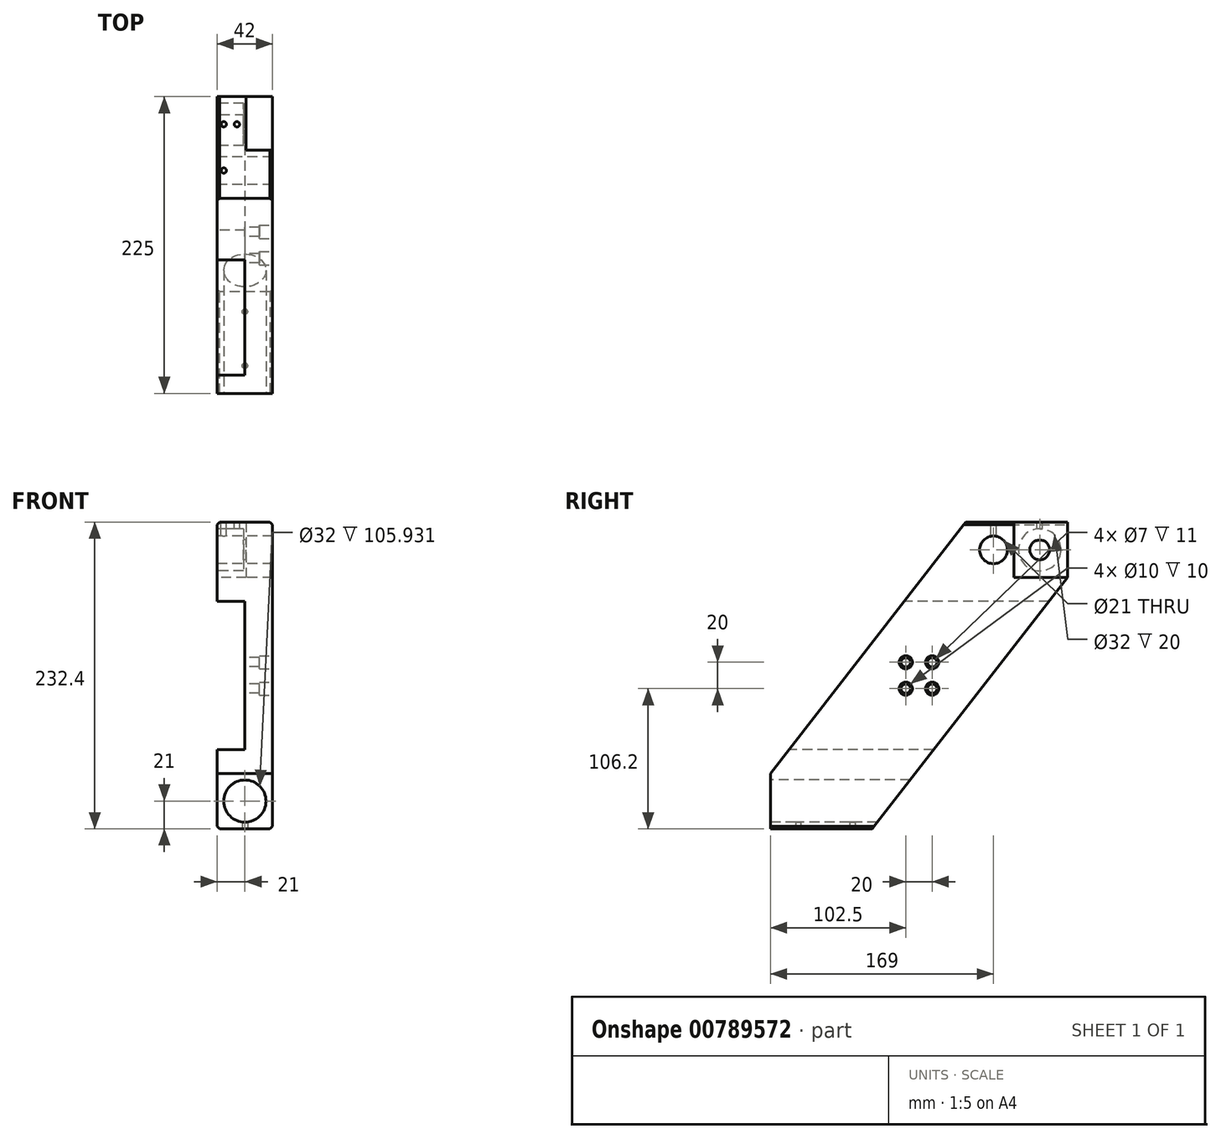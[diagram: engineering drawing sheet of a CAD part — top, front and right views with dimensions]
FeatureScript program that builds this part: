
annotation { "Feature Type Name" : "Feature", "Feature Type Description" : "" }
export const myFeature = defineFeature(function(context is Context, id is Id, definition is map)
    precondition{}
    {
        {
            var Q0;
            Q0=qCreatedBy(makeId("Right.planeOp"),FACE);
            var sketch = newSketch(context, id + "F0", { "sketchPlane" : qUnion([Q0])});
            skLineSegment(sketch, "E0.bottom", {"start": v(112.5, 116.2) * mm, "end": v(35.5, 116.2) * mm});
            skLineSegment(sketch, "E0.top", {"start": v(112.5, -116.2) * mm, "end": v(70.5, -116.2) * mm});
            skLineSegment(sketch, "E0.left", {"start": v(112.5, 116.2) * mm, "end": v(112.5, 74.2) * mm});
            skLineSegment(sketch, "E0.right", {"start": v(-112.5, 116.2) * mm, "end": v(-112.5, 74.2) * mm});
            skCircle(sketch, "E1", {"center": v(56.5, 95.2) * mm, "radius": 10.5 * mm});
            skCircle(sketch, "E2", {"center": v(-91.5, 95.2) * mm, "radius": 10.5 * mm});
            skPoint(sketch, "E3", {"position": v(0, 0) * mm});
            skPoint(sketch, "E4.start.orphan", {"position": v(112.5, 116.2) * mm});
            skPoint(sketch, "E5.trimOffspring.end.orphan", {"position": v(-112.5, 116.2) * mm});
            skCircle(sketch, "E6", {"center": v(91.5, 95.2) * mm, "radius": 7.5 * mm});
            skPoint(sketch, "E7", {"position": v(-35.5, -116.2) * mm});
            skPoint(sketch, "E8", {"position": v(70.5, -116.2) * mm});
            skPoint(sketch, "E9", {"position": v(112.5, -74.2) * mm});
            skPoint(sketch, "E10", {"position": v(-112.5, -74.2) * mm});
            skPoint(sketch, "E11", {"position": v(112.5, 74.2) * mm});
            skPoint(sketch, "E12", {"position": v(-112.5, 74.2) * mm});
            skLineSegment(sketch, "E13", {"start": v(112.5, 74.2) * mm, "end": v(-35.5, -116.2) * mm});
            skLineSegment(sketch, "E14", {"start": v(70.5, -116.2) * mm, "end": v(-112.5, 74.2) * mm});
            skPoint(sketch, "E15", {"position": v(35.5, 116.2) * mm});
            skPoint(sketch, "E16", {"position": v(-70.5, 116.2) * mm});
            skLineSegment(sketch, "E17", {"start": v(35.5, 116.2) * mm, "end": v(-112.5, -74.2) * mm});
            skLineSegment(sketch, "E18", {"start": v(112.5, -74.2) * mm, "end": v(-70.5, 116.2) * mm});
            skLineSegment(sketch, "E19.trimOffspring", {"start": v(-70.5, 116.2) * mm, "end": v(-112.5, 116.2) * mm});
            skLineSegment(sketch, "E20.trimOffspring", {"start": v(-112.5, -74.2) * mm, "end": v(-112.5, -116.2) * mm});
            skLineSegment(sketch, "E21.trimOffspring", {"start": v(-35.5, -116.2) * mm, "end": v(-112.5, -116.2) * mm});
            skLineSegment(sketch, "E22.trimOffspring", {"start": v(112.5, -74.2) * mm, "end": v(112.5, -116.2) * mm});
            skPoint(sketch, "E23", {"position": v(10, 10) * mm});
            skPoint(sketch, "E24", {"position": v(10, -10) * mm});
            skPoint(sketch, "E25", {"position": v(-10, -10) * mm});
            skPoint(sketch, "E26", {"position": v(-10, 10) * mm});
            skCircle(sketch, "E27", {"center": v(10, 10) * mm, "radius": 3.5 * mm});
            skCircle(sketch, "E28", {"center": v(-10, 10) * mm, "radius": 3.5 * mm});
            skCircle(sketch, "E29", {"center": v(10, -10) * mm, "radius": 3.5 * mm});
            skCircle(sketch, "E30", {"center": v(-10, -10) * mm, "radius": 3.5 * mm});
            skLineSegment(sketch, "E31", {"start": v(-112.5, 116.2) * mm, "end": v(112.5, -116.2) * mm});
            skLineSegment(sketch, "E32", {"start": v(-112.5, -116.2) * mm, "end": v(112.5, 116.2) * mm});
            skSolve(sketch);
        }
        {
            var Q0;
            {var subQ5=sQuery(id+"F0.wireOp",EDGE,"E20.trimOffspring");Q0=makeQuery(id+"F0.imprint","IMPRINT",FACE,{"disambiguationData":[TD([[makeQuery(id+"F0.imprint","IMPRINT",EDGE,{"derivedFrom":subQ5}),1.0]])]});}
            var Q1;
            {var subQ0=sQuery(id+"F0.wireOp",EDGE,"E21.trimOffspring");Q1=makeQuery(id+"F0.imprint","IMPRINT",FACE,{"disambiguationData":[TD([[makeQuery(id+"F0.imprint","IMPRINT",EDGE,{"derivedFrom":subQ0}),-1.0]])]});}
            var Q2;
            {var subQ6=sQuery(id+"F0.wireOp",EDGE,"E17");var subQ7=sQuery(id+"F0.wireOp",EDGE,"E14");var subQ8=makeQuery(id+"F0.imprint","INTERSECT",VERTEX,{"derivedFrom":[subQ7,subQ6]});Q2=makeQuery(id+"F0.imprint","IMPRINT",FACE,{"disambiguationData":[TD([[makeQuery(id+"F0.imprint","IMPRINT",EDGE,{"disambiguationData":[TD([[subQ8,1.0]])],"derivedFrom":subQ7}),-1.0]])]});}
            var Q3;
            {var subQ4=sQuery(id+"F0.wireOp",EDGE,"E14");var subQ5=sQuery(id+"F0.wireOp",EDGE,"E13");var subQ6=makeQuery(id+"F0.imprint","INTERSECT",VERTEX,{"derivedFrom":[subQ5,subQ4]});Q3=makeQuery(id+"F0.imprint","IMPRINT",FACE,{"disambiguationData":[TD([[makeQuery(id+"F0.imprint","IMPRINT",EDGE,{"disambiguationData":[TD([[subQ6,1.0]])],"derivedFrom":subQ5}),-1.0]])]});}
            var Q4;
            {var subQ8=sQuery(id+"F0.wireOp",EDGE,"E18");var subQ9=sQuery(id+"F0.wireOp",EDGE,"E17");var subQ10=makeQuery(id+"F0.imprint","INTERSECT",VERTEX,{"derivedFrom":[subQ9,subQ8]});Q4=makeQuery(id+"F0.imprint","IMPRINT",FACE,{"disambiguationData":[TD([[makeQuery(id+"F0.imprint","IMPRINT",EDGE,{"disambiguationData":[TD([[subQ10,-1.0]])],"derivedFrom":subQ9}),1.0]])]});}
            var Q5;
            {var subQ4=sQuery(id+"F0.wireOp",EDGE,"E13");var subQ6=sQuery(id+"F0.wireOp",EDGE,"E18");var subQ7=makeQuery(id+"F0.imprint","INTERSECT",VERTEX,{"derivedFrom":[subQ4,subQ6]});Q5=makeQuery(id+"F0.imprint","IMPRINT",FACE,{"disambiguationData":[TD([[makeQuery(id+"F0.imprint","IMPRINT",EDGE,{"disambiguationData":[TD([[subQ7,-1.0]])],"derivedFrom":subQ4}),-1.0]])]});}
            var Q6;
            {var subQ1=sQuery(id+"F0.wireOp",EDGE,"E0.left");Q6=makeQuery(id+"F0.imprint","IMPRINT",FACE,{"disambiguationData":[TD([[makeQuery(id+"F0.imprint","IMPRINT",EDGE,{"derivedFrom":subQ1}),-1.0]])]});}
            var Q7;
            {var subQ1=sQuery(id+"F0.wireOp",EDGE,"E0.bottom");Q7=makeQuery(id+"F0.imprint","IMPRINT",FACE,{"disambiguationData":[TD([[makeQuery(id+"F0.imprint","IMPRINT",EDGE,{"derivedFrom":subQ1}),1.0]])]});}
            extrude(context, id + "F1", {"entities" : qUnion([Q0, Q1, Q2, Q3, Q4, Q5, Q6, Q7]), "depth" : 42 * mm, "offsetDistance" : 25 * mm});
        }
        {
            var Q0;
            Q0=makeQuery(id+"F1.opExtrude","CAP_FACE",FACE,{"disambiguationData":[OSD([sQuery(id+"F0.wireOp",EDGE,"E0.bottom"),sQuery(id+"F0.wireOp",EDGE,"E0.left"),sQuery(id+"F0.wireOp",EDGE,"E1"),sQuery(id+"F0.wireOp",EDGE,"E6"),sQuery(id+"F0.wireOp",EDGE,"E13"),sQuery(id+"F0.wireOp",EDGE,"E17"),sQuery(id+"F0.wireOp",EDGE,"E20.trimOffspring"),sQuery(id+"F0.wireOp",EDGE,"E21.trimOffspring"),sQuery(id+"F0.wireOp",EDGE,"E27"),sQuery(id+"F0.wireOp",EDGE,"E28"),sQuery(id+"F0.wireOp",EDGE,"E29"),sQuery(id+"F0.wireOp",EDGE,"E30")])],"isStart":false});
            var sketch = newSketch(context, id + "F2", { "sketchPlane" : qUnion([Q0])});
            skCircle(sketch, "E33", {"center": v(-10, 10) * mm, "radius": 5 * mm});
            skCircle(sketch, "E34", {"center": v(10, 10) * mm, "radius": 5 * mm});
            skCircle(sketch, "E35", {"center": v(10, -10) * mm, "radius": 5 * mm});
            skCircle(sketch, "E36", {"center": v(-10, -10) * mm, "radius": 5 * mm});
            skSolve(sketch);
        }
        {
            var Q0;
            Q0=makeQuery(id+"F2.imprint","IMPRINT",FACE,{"disambiguationData":[TD([[makeQuery(id+"F2.imprint","IMPRINT",EDGE,{"derivedFrom":sQuery(id+"F2.wireOp",EDGE,"E35")}),1.0]])]});
            var Q1;
            Q1=makeQuery(id+"F2.imprint","IMPRINT",FACE,{"disambiguationData":[TD([[makeQuery(id+"F2.imprint","IMPRINT",EDGE,{"derivedFrom":sQuery(id+"F2.wireOp",EDGE,"E36")}),1.0]])]});
            var Q2;
            Q2=makeQuery(id+"F2.imprint","IMPRINT",FACE,{"disambiguationData":[TD([[makeQuery(id+"F2.imprint","IMPRINT",EDGE,{"derivedFrom":sQuery(id+"F2.wireOp",EDGE,"E33")}),1.0]])]});
            var Q3;
            Q3=makeQuery(id+"F2.imprint","IMPRINT",FACE,{"disambiguationData":[TD([[makeQuery(id+"F2.imprint","IMPRINT",EDGE,{"derivedFrom":sQuery(id+"F2.wireOp",EDGE,"E34")}),1.0]])]});
            extrude(context, id + "F3", {"entities" : qUnion([Q0, Q1, Q2, Q3]), "operationType" : NewBodyOperationType.REMOVE, "oppositeDirection" : true, "depth" : 10 * mm, "offsetDistance" : 25 * mm});
        }
        {
            var Q0;
            Q0=makeQuery(id+"F1.opExtrude","CAP_FACE",FACE,{"disambiguationData":[OSD([sQuery(id+"F0.wireOp",EDGE,"E0.bottom"),sQuery(id+"F0.wireOp",EDGE,"E0.left"),sQuery(id+"F0.wireOp",EDGE,"E1"),sQuery(id+"F0.wireOp",EDGE,"E6"),sQuery(id+"F0.wireOp",EDGE,"E13"),sQuery(id+"F0.wireOp",EDGE,"E17"),sQuery(id+"F0.wireOp",EDGE,"E20.trimOffspring"),sQuery(id+"F0.wireOp",EDGE,"E21.trimOffspring"),sQuery(id+"F0.wireOp",EDGE,"E27"),sQuery(id+"F0.wireOp",EDGE,"E28"),sQuery(id+"F0.wireOp",EDGE,"E29"),sQuery(id+"F0.wireOp",EDGE,"E30")])],"isStart":false});
            var sketch = newSketch(context, id + "F4", { "sketchPlane" : qUnion([Q0])});
            skLineSegment(sketch, "E37", {"start": v(72, 116.2) * mm, "end": v(72, 74.2) * mm});
            skLineSegment(sketch, "E38", {"start": v(72, 74.2) * mm, "end": v(145, 74.2) * mm});
            skLineSegment(sketch, "E39", {"start": v(145, 74.2) * mm, "end": v(145, 116.2) * mm});
            skLineSegment(sketch, "E40", {"start": v(145, 116.2) * mm, "end": v(72, 116.2) * mm});
            skSolve(sketch);
        }
        {
            var Q0;
            {var subQ2=sQuery(id+"F4.wireOp",EDGE,"E37");Q0=makeQuery(id+"F4.imprint","IMPRINT",FACE,{"disambiguationData":[TD([[makeQuery(id+"F4.imprint","IMPRINT",EDGE,{"derivedFrom":subQ2}),1.0]])]});}
            extrude(context, id + "F5", {"entities" : qUnion([Q0]), "operationType" : NewBodyOperationType.REMOVE, "oppositeDirection" : true, "depth" : 20 * mm, "offsetDistance" : 25 * mm});
        }
        {
            var Q0;
            Q0=makeQuery(id+"F1.opExtrude","CAP_FACE",FACE,{"disambiguationData":[OSD([sQuery(id+"F0.wireOp",EDGE,"E0.bottom"),sQuery(id+"F0.wireOp",EDGE,"E0.left"),sQuery(id+"F0.wireOp",EDGE,"E1"),sQuery(id+"F0.wireOp",EDGE,"E6"),sQuery(id+"F0.wireOp",EDGE,"E13"),sQuery(id+"F0.wireOp",EDGE,"E17"),sQuery(id+"F0.wireOp",EDGE,"E20.trimOffspring"),sQuery(id+"F0.wireOp",EDGE,"E21.trimOffspring"),sQuery(id+"F0.wireOp",EDGE,"E27"),sQuery(id+"F0.wireOp",EDGE,"E28"),sQuery(id+"F0.wireOp",EDGE,"E29"),sQuery(id+"F0.wireOp",EDGE,"E30")])],"isStart":true});
            var sketch = newSketch(context, id + "F6", { "sketchPlane" : qUnion([Q0])});
            skLineSegment(sketch, "E41", {"start": v(-98.5, 56.2) * mm, "end": v(11.14, 56.2) * mm});
            skLineSegment(sketch, "E42", {"start": v(-11.14, -56.2) * mm, "end": v(112.5, -56.2) * mm});
            skSolve(sketch);
        }
        {
            var Q0;
            {var subQ1=sQuery(id+"F6.wireOp",EDGE,"E41");Q0=makeQuery(id+"F6.imprint","IMPRINT",FACE,{"disambiguationData":[TD([[makeQuery(id+"F6.imprint","IMPRINT",EDGE,{"derivedFrom":subQ1}),-1.0]])]});}
            extrude(context, id + "F7", {"entities" : qUnion([Q0]), "operationType" : NewBodyOperationType.REMOVE, "oppositeDirection" : true, "depth" : 21 * mm, "offsetDistance" : 25 * mm});
        }
        {
            var Q0;
            Q0=makeQuery(id+"F1.opExtrude","SWEPT_FACE",FACE,{"disambiguationData":[OSD([sQuery(id+"F0.wireOp",EDGE,"E20.trimOffspring")])]});
            var sketch = newSketch(context, id + "F8", { "sketchPlane" : qUnion([Q0])});
            skPoint(sketch, "E43", {"position": v(21, -95.2) * mm});
            skPoint(sketch, "E43.positionSnap0", {"position": v(42, -95.2) * mm});
            skCircle(sketch, "E44", {"center": v(21, -95.2) * mm, "radius": 16 * mm});
            skSolve(sketch);
        }
        {
            var Q0;
            Q0=makeQuery(id+"F8.imprint","IMPRINT",FACE,{"disambiguationData":[TD([[makeQuery(id+"F8.imprint","IMPRINT",EDGE,{"derivedFrom":sQuery(id+"F8.wireOp",EDGE,"E44")}),1.0]])]});
            extrude(context, id + "F9", {"entities" : qUnion([Q0]), "operationType" : NewBodyOperationType.REMOVE, "oppositeDirection" : true, "depth" : 150 * mm, "offsetDistance" : 25 * mm});
        }
        {
            var Q0;
            Q0=makeQuery(id+"F1.opExtrude","CAP_EDGE",EDGE,{"disambiguationData":[OSD([sQuery(id+"F0.wireOp",EDGE,"E21.trimOffspring")])],"isStart":false});
            var Q1;
            Q1=makeQuery(id+"F5.boolean.opBoolean","COPY",EDGE,{"derivedFrom":makeQuery(id+"F5.opExtrude","CAP_EDGE",EDGE,{"disambiguationData":[OSD([sQuery(id+"F4.wireOp",EDGE,"E38")])],"isStart":true})});
            var Q2;
            Q2=makeQuery(id+"F5.boolean.opBoolean","COPY",EDGE,{"derivedFrom":makeQuery(id+"F5.opExtrude","CAP_EDGE",EDGE,{"disambiguationData":[OSD([sQuery(id+"F4.wireOp",EDGE,"E37")])],"isStart":true})});
            var Q3;
            Q3=makeQuery(id+"F1.opExtrude","CAP_EDGE",EDGE,{"disambiguationData":[OSD([sQuery(id+"F0.wireOp",EDGE,"E0.bottom")])],"isStart":false});
            var Q4;
            Q4=makeQuery(id+"F1.opExtrude","CAP_EDGE",EDGE,{"disambiguationData":[OSD([sQuery(id+"F0.wireOp",EDGE,"E21.trimOffspring")])],"isStart":true});
            var Q5;
            Q5=makeQuery(id+"F7.boolean.opBoolean","COPY",EDGE,{"derivedFrom":makeQuery(id+"F7.opExtrude","CAP_EDGE",EDGE,{"disambiguationData":[OSD([sQuery(id+"F6.wireOp",EDGE,"E42")])],"isStart":true})});
            var Q6;
            Q6=makeQuery(id+"F7.boolean.opBoolean","COPY",EDGE,{"derivedFrom":makeQuery(id+"F7.opExtrude","CAP_EDGE",EDGE,{"disambiguationData":[OSD([sQuery(id+"F6.wireOp",EDGE,"E41")])],"isStart":true})});
            var Q7;
            Q7=makeQuery(id+"F1.opExtrude","CAP_EDGE",EDGE,{"disambiguationData":[OSD([sQuery(id+"F0.wireOp",EDGE,"E0.bottom")])],"isStart":true});
            chamfer(context, id + "F10", {"entities" : qUnion([Q0, Q1, Q2, Q3, Q4, Q5, Q6, Q7]), "width" : 2 * mm, "tangentPropagation" : true});
        }
        {
            var Q0;
            Q0=makeQuery(id+"F1.opExtrude","SWEPT_FACE",FACE,{"disambiguationData":[OSD([sQuery(id+"F0.wireOp",EDGE,"E21.trimOffspring")])]});
            var sketch = newSketch(context, id + "F11", { "sketchPlane" : qUnion([Q0])});
            skPoint(sketch, "E45", {"position": v(21, 91.5) * mm});
            skPoint(sketch, "E45.positionSnap0", {"position": v(21, 112.5) * mm});
            skPoint(sketch, "E46", {"position": v(21, 50.5) * mm});
            skPoint(sketch, "E46.positionSnap0", {"position": v(21, 35.5) * mm});
            skCircle(sketch, "E47", {"center": v(21, 50.5) * mm, "radius": 2 * mm});
            skCircle(sketch, "E48", {"center": v(21, 91.5) * mm, "radius": 2 * mm});
            skSolve(sketch);
        }
        {
            var Q0;
            Q0 = qSketchRegion(id + "F11", true);
            extrude(context, id + "F12", {"entities" : qUnion([Q0]), "operationType" : NewBodyOperationType.REMOVE, "oppositeDirection" : true, "depth" : 25 * mm, "offsetDistance" : 25 * mm});
        }
        {
            var Q0;
            Q0=makeQuery(id+"F1.opExtrude","SWEPT_FACE",FACE,{"disambiguationData":[OSD([sQuery(id+"F0.wireOp",EDGE,"E0.bottom")])]});
            var sketch = newSketch(context, id + "F13", { "sketchPlane" : qUnion([Q0])});
            skPoint(sketch, "E49", {"position": v(5, 91.5) * mm});
            skPoint(sketch, "E49.positionSnap0", {"position": v(5, 112.5) * mm});
            skCircle(sketch, "E50", {"center": v(5, 91.5) * mm, "radius": 2 * mm});
            skPoint(sketch, "E51", {"position": v(15, 56.5) * mm});
            skPoint(sketch, "E52", {"position": v(5, 56.5) * mm});
            skCircle(sketch, "E53", {"center": v(15, 91.5) * mm, "radius": 2 * mm});
            skCircle(sketch, "E54", {"center": v(5, 56.5) * mm, "radius": 2 * mm});
            skSolve(sketch);
        }
        {
            var Q0;
            Q0=makeQuery(id+"F13.imprint","IMPRINT",FACE,{"disambiguationData":[TD([[makeQuery(id+"F13.imprint","IMPRINT",EDGE,{"derivedFrom":sQuery(id+"F13.wireOp",EDGE,"E54")}),1.0]])]});
            var Q1;
            Q1=makeQuery(id+"F13.imprint","IMPRINT",FACE,{"disambiguationData":[TD([[makeQuery(id+"F13.imprint","IMPRINT",EDGE,{"derivedFrom":sQuery(id+"F13.wireOp",EDGE,"E53")}),1.0]])]});
            var Q2;
            Q2=makeQuery(id+"F13.imprint","IMPRINT",FACE,{"disambiguationData":[TD([[makeQuery(id+"F13.imprint","IMPRINT",EDGE,{"derivedFrom":sQuery(id+"F13.wireOp",EDGE,"E50")}),1.0]])]});
            extrude(context, id + "F14", {"entities" : qUnion([Q0, Q1, Q2]), "operationType" : NewBodyOperationType.REMOVE, "oppositeDirection" : true, "depth" : 25 * mm, "offsetDistance" : 25 * mm});
        }
        {
            var Q0;
            {var subQ0=sQuery(id+"F0.wireOp",EDGE,"E1");var subQ1=sQuery(id+"F0.wireOp",EDGE,"E0.left");var subQ2=sQuery(id+"F0.wireOp",EDGE,"E6");var subQ3=sQuery(id+"F0.wireOp",EDGE,"E0.bottom");var subQ4=sQuery(id+"F0.wireOp",EDGE,"E13");var subQ5=sQuery(id+"F0.wireOp",EDGE,"E17");Q0=makeQuery(id+"F7.boolean.opBoolean","SPLIT",FACE,{"disambiguationData":[TD([makeQuery(id+"F1.opExtrude","SWEPT_FACE",FACE,{"disambiguationData":[OSD([subQ3])]})])],"derivedFrom":makeQuery(id+"F1.opExtrude","CAP_FACE",FACE,{"disambiguationData":[OSD([subQ3,subQ1,subQ0,subQ2,subQ4,subQ5,sQuery(id+"F0.wireOp",EDGE,"E20.trimOffspring"),sQuery(id+"F0.wireOp",EDGE,"E21.trimOffspring"),sQuery(id+"F0.wireOp",EDGE,"E27"),sQuery(id+"F0.wireOp",EDGE,"E28"),sQuery(id+"F0.wireOp",EDGE,"E29"),sQuery(id+"F0.wireOp",EDGE,"E30")])],"isStart":true})});}
            var sketch = newSketch(context, id + "F15", { "sketchPlane" : qUnion([Q0])});
            skPoint(sketch, "E55", {"position": v(-91.5, 95.2) * mm});
            skCircle(sketch, "E56", {"center": v(-91.5, 95.2) * mm, "radius": 16 * mm});
            skSolve(sketch);
        }
        {
            var Q0;
            Q0=makeQuery(id+"F15.imprint","IMPRINT",FACE,{"disambiguationData":[TD([[makeQuery(id+"F15.imprint","IMPRINT",EDGE,{"derivedFrom":sQuery(id+"F15.wireOp",EDGE,"E56")}),1.0]])]});
            extrude(context, id + "F16", {"entities" : qUnion([Q0]), "operationType" : NewBodyOperationType.REMOVE, "oppositeDirection" : true, "depth" : 20 * mm, "offsetDistance" : 25 * mm});
        }
    });
